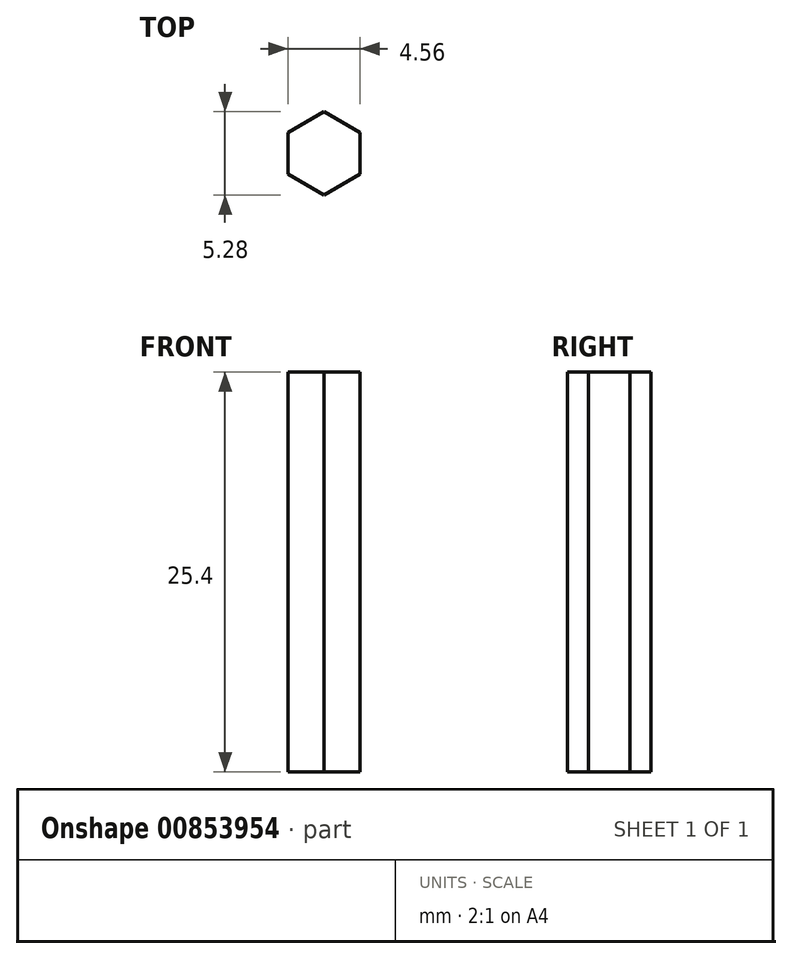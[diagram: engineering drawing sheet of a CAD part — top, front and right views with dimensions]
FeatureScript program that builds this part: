
annotation { "Feature Type Name" : "Feature", "Feature Type Description" : "" }
export const myFeature = defineFeature(function(context is Context, id is Id, definition is map)
    precondition{}
    {
        {
            var Q0;
            Q0=qCreatedBy(makeId("Top.planeOp"),FACE);
            var sketch = newSketch(context, id + "F0", { "sketchPlane" : qUnion([Q0])});
            skCircle(sketch, "E0.cCircle", {"center": v(0, 0) * mm, "radius": 2.28 * mm, "construction": true});
            skLineSegment(sketch, "E0.0", {"start": v(2.28, 1.32) * mm, "end": v(2.28, -1.32) * mm});
            skLineSegment(sketch, "E0.1", {"start": v(2.28, -1.32) * mm, "end": v(0, -2.64) * mm});
            skLineSegment(sketch, "E0.2", {"start": v(0, -2.64) * mm, "end": v(-2.28, -1.32) * mm});
            skLineSegment(sketch, "E0.3", {"start": v(-2.28, -1.32) * mm, "end": v(-2.28, 1.32) * mm});
            skLineSegment(sketch, "E0.4", {"start": v(-2.28, 1.32) * mm, "end": v(0, 2.64) * mm});
            skLineSegment(sketch, "E0.5", {"start": v(0, 2.64) * mm, "end": v(2.28, 1.32) * mm});
            skPoint(sketch, "E0.0.midPoint", {"position": v(2.28, 0) * mm});
            skSolve(sketch);
        }
        {
            var Q0;
            Q0=makeQuery(id+"F0.imprint","IMPRINT",FACE,{"disambiguationData":[TD([[makeQuery(id+"F0.imprint","IMPRINT",EDGE,{"derivedFrom":sQuery(id+"F0.wireOp",EDGE,"E0.0")}),-1.0]])]});
            extrude(context, id + "F1", {"entities" : qUnion([Q0]), "depth" : 25.4 * mm, "offsetDistance" : 25.4 * mm});
        }
    });
